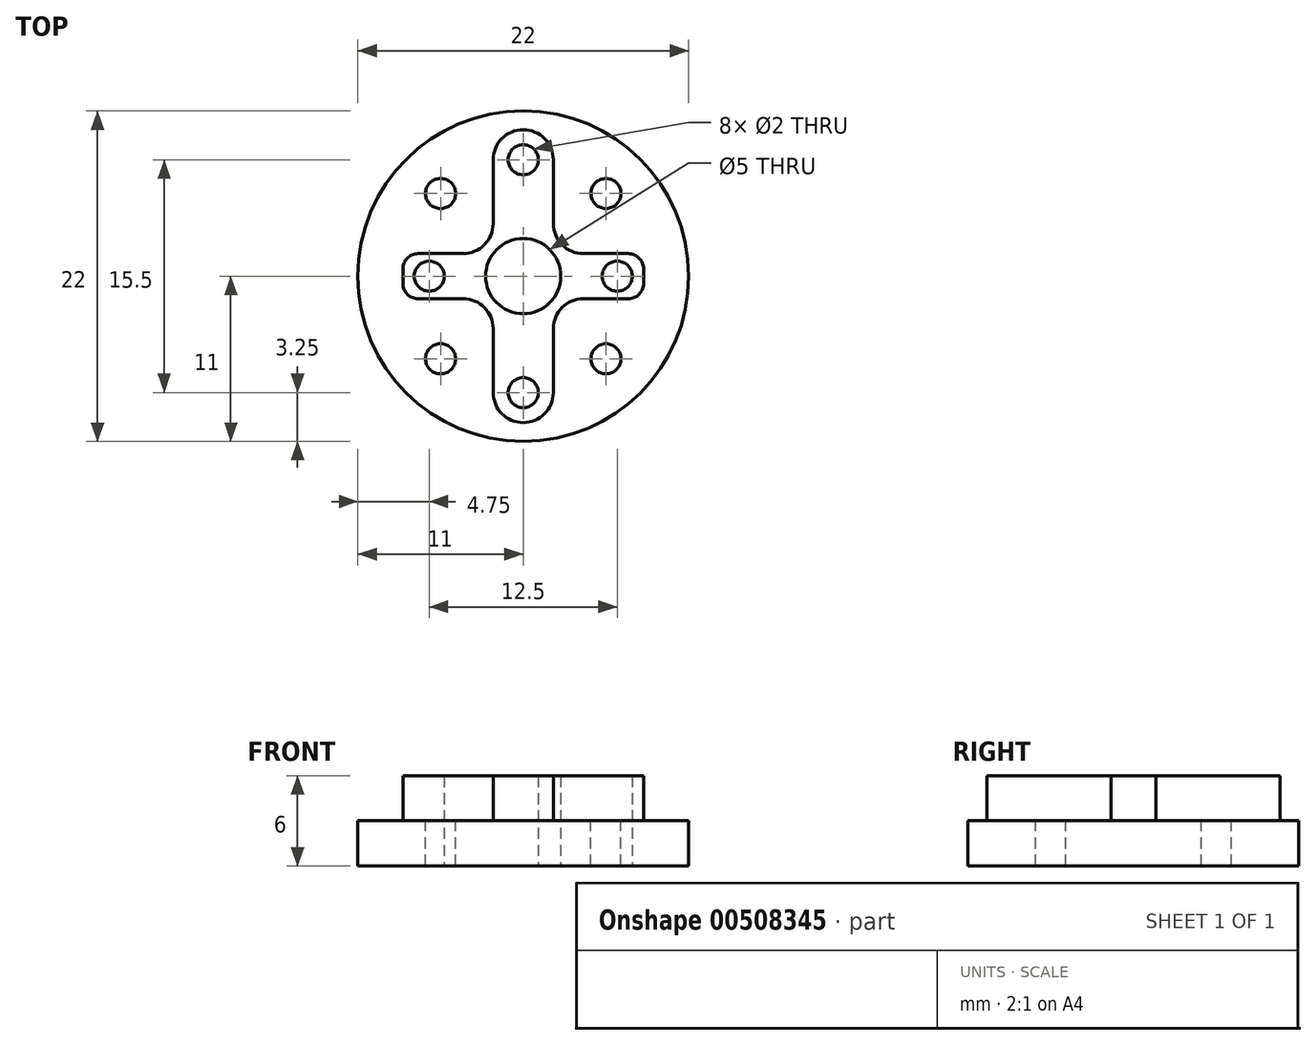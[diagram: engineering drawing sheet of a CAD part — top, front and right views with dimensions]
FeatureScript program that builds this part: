
annotation { "Feature Type Name" : "Feature", "Feature Type Description" : "" }
export const myFeature = defineFeature(function(context is Context, id is Id, definition is map)
    precondition{}
    {
        {
            var Q0;
            Q0=qCreatedBy(makeId("Top.planeOp"),FACE);
            var sketch = newSketch(context, id + "F0", { "sketchPlane" : qUnion([Q0])});
            skLineSegment(sketch, "E0", {"start": v(0, 15) * mm, "end": v(0, -15) * mm, "construction": true});
            skLineSegment(sketch, "E1", {"start": v(-15, 0) * mm, "end": v(15, 0) * mm, "construction": true});
            skCircle(sketch, "E2", {"center": v(0, 0) * mm, "radius": 2.5 * mm});
            skCircle(sketch, "E3", {"center": v(0, 7.75) * mm, "radius": 1 * mm});
            skCircle(sketch, "E4", {"center": v(6.25, 0) * mm, "radius": 1 * mm});
            skCircle(sketch, "E5.MirrorC", {"center": v(-6.25, 0) * mm, "radius": 1 * mm});
            skCircle(sketch, "E6.MirrorC", {"center": v(0, -7.75) * mm, "radius": 1 * mm});
            skLineSegment(sketch, "E7", {"start": v(2, 3.5) * mm, "end": v(2, 7.75) * mm});
            skLineSegment(sketch, "E8", {"start": v(4, 1.5) * mm, "end": v(7, 1.5) * mm});
            skPoint(sketch, "E9.visualSharp", {"position": v(2, 1.5) * mm});
            skArc(sketch, "E9.filletArc", {"start": v(2, 3.5) * mm, "mid": v(2.59, 2.09) * mm, "end": v(4, 1.5) * mm});
            skLineSegment(sketch, "E10.MirrorCS", {"start": v(-2, 3.5) * mm, "end": v(-2, 7.75) * mm});
            skArc(sketch, "E11.MirrorCS", {"start": v(-2, 3.5) * mm, "mid": v(-2.59, 2.09) * mm, "end": v(-4, 1.5) * mm});
            skLineSegment(sketch, "E12.MirrorCS", {"start": v(4, -1.5) * mm, "end": v(7, -1.5) * mm});
            skArc(sketch, "E13.MirrorCS", {"start": v(2, -3.5) * mm, "mid": v(2.59, -2.09) * mm, "end": v(4, -1.5) * mm});
            skArc(sketch, "E14.MirrorCS", {"start": v(-2, -3.5) * mm, "mid": v(-2.59, -2.09) * mm, "end": v(-4, -1.5) * mm});
            skLineSegment(sketch, "E15", {"start": v(0, 9.75) * mm, "end": v(0, 9.75) * mm});
            skPoint(sketch, "E16.visualSharp", {"position": v(2, 9.75) * mm});
            skArc(sketch, "E16.filletArc", {"start": v(2, 7.75) * mm, "mid": v(1.41, 9.16) * mm, "end": v(0, 9.75) * mm});
            skPoint(sketch, "E17.visualSharp", {"position": v(-2, 9.75) * mm});
            skArc(sketch, "E17.filletArc", {"start": v(0, 9.75) * mm, "mid": v(-1.41, 9.16) * mm, "end": v(-2, 7.75) * mm});
            skArc(sketch, "E18.MirrorCS", {"start": v(0, -9.75) * mm, "mid": v(-1.41, -9.16) * mm, "end": v(-2, -7.75) * mm});
            skArc(sketch, "E19.MirrorCS", {"start": v(2, -7.75) * mm, "mid": v(1.41, -9.16) * mm, "end": v(0, -9.75) * mm});
            skLineSegment(sketch, "E20.MirrorCS", {"start": v(2, -3.5) * mm, "end": v(2, -7.75) * mm});
            skLineSegment(sketch, "E21.MirrorCS", {"start": v(-2, -3.5) * mm, "end": v(-2, -7.75) * mm});
            skLineSegment(sketch, "E22", {"start": v(8, -0.5) * mm, "end": v(8, 0.5) * mm});
            skPoint(sketch, "E23.visualSharp", {"position": v(8, 1.5) * mm});
            skArc(sketch, "E23.filletArc", {"start": v(8, 0.5) * mm, "mid": v(7.7, 1.2) * mm, "end": v(7, 1.5) * mm});
            skPoint(sketch, "E24.visualSharp", {"position": v(8, -1.5) * mm});
            skArc(sketch, "E24.filletArc", {"start": v(7, -1.5) * mm, "mid": v(7.7, -1.2) * mm, "end": v(8, -0.5) * mm});
            skLineSegment(sketch, "E25.MirrorCS", {"start": v(-4, 1.5) * mm, "end": v(-7, 1.5) * mm});
            skLineSegment(sketch, "E26.MirrorCS", {"start": v(-8, -0.5) * mm, "end": v(-8, 0.5) * mm});
            skArc(sketch, "E27.MirrorCS", {"start": v(-7, -1.5) * mm, "mid": v(-7.7, -1.2) * mm, "end": v(-8, -0.5) * mm});
            skLineSegment(sketch, "E28.MirrorCS", {"start": v(-4, -1.5) * mm, "end": v(-7, -1.5) * mm});
            skArc(sketch, "E29.MirrorCS", {"start": v(-8, 0.5) * mm, "mid": v(-7.7, 1.2) * mm, "end": v(-7, 1.5) * mm});
            skSolve(sketch);
        }
        {
            var Q0;
            Q0=makeQuery(id+"F0.imprint","IMPRINT",FACE,{"disambiguationData":[TD([[makeQuery(id+"F0.imprint","IMPRINT",EDGE,{"derivedFrom":sQuery(id+"F0.wireOp",EDGE,"E2")}),-1.0]])]});
            extrude(context, id + "F1", {"entities" : qUnion([Q0]), "depth" : 3 * mm, "offsetDistance" : 25 * mm});
        }
        {
            var Q0;
            Q0=makeQuery(id+"F1.opExtrude","CAP_FACE",FACE,{"disambiguationData":[OSD([sQuery(id+"F0.wireOp",EDGE,"E2"),sQuery(id+"F0.wireOp",EDGE,"E3"),sQuery(id+"F0.wireOp",EDGE,"E4"),sQuery(id+"F0.wireOp",EDGE,"E5.MirrorC"),sQuery(id+"F0.wireOp",EDGE,"E6.MirrorC"),sQuery(id+"F0.wireOp",EDGE,"E7"),sQuery(id+"F0.wireOp",EDGE,"E8"),sQuery(id+"F0.wireOp",EDGE,"E9.filletArc"),sQuery(id+"F0.wireOp",EDGE,"E10.MirrorCS"),sQuery(id+"F0.wireOp",EDGE,"E11.MirrorCS"),sQuery(id+"F0.wireOp",EDGE,"E12.MirrorCS"),sQuery(id+"F0.wireOp",EDGE,"E13.MirrorCS"),sQuery(id+"F0.wireOp",EDGE,"E14.MirrorCS"),sQuery(id+"F0.wireOp",EDGE,"E18.MirrorCS"),sQuery(id+"F0.wireOp",EDGE,"E19.MirrorCS"),sQuery(id+"F0.wireOp",EDGE,"E16.filletArc"),sQuery(id+"F0.wireOp",EDGE,"E17.filletArc"),sQuery(id+"F0.wireOp",EDGE,"E20.MirrorCS"),sQuery(id+"F0.wireOp",EDGE,"E21.MirrorCS"),sQuery(id+"F0.wireOp",EDGE,"E22"),sQuery(id+"F0.wireOp",EDGE,"E23.filletArc"),sQuery(id+"F0.wireOp",EDGE,"E24.filletArc"),sQuery(id+"F0.wireOp",EDGE,"E25.MirrorCS"),sQuery(id+"F0.wireOp",EDGE,"E26.MirrorCS"),sQuery(id+"F0.wireOp",EDGE,"E27.MirrorCS"),sQuery(id+"F0.wireOp",EDGE,"E28.MirrorCS"),sQuery(id+"F0.wireOp",EDGE,"E29.MirrorCS")])],"isStart":true});
            var sketch = newSketch(context, id + "F2", { "sketchPlane" : qUnion([Q0])});
            skCircle(sketch, "E30", {"center": v(0, 0) * mm, "radius": 11 * mm});
            skLineSegment(sketch, "E31", {"start": v(0, 16.96) * mm, "end": v(0, -14.39) * mm, "construction": true});
            skCircle(sketch, "E32", {"center": v(-5.5, 5.5) * mm, "radius": 1 * mm});
            skLineSegment(sketch, "E33", {"start": v(-12.82, 0) * mm, "end": v(13.52, 0) * mm, "construction": true});
            skPoint(sketch, "E33.endSnap0", {"position": v(8, 0) * mm});
            skCircle(sketch, "E34.MirrorC", {"center": v(5.5, 5.5) * mm, "radius": 1 * mm});
            skCircle(sketch, "E35.MirrorC", {"center": v(5.5, -5.5) * mm, "radius": 1 * mm});
            skCircle(sketch, "E36.MirrorC", {"center": v(-5.5, -5.5) * mm, "radius": 1 * mm});
            skSolve(sketch);
        }
        {
            var Q0;
            Q0=makeQuery(id+"F2.imprint","IMPRINT",FACE,{"disambiguationData":[TD([[makeQuery(id+"F2.imprint","IMPRINT",EDGE,{"derivedFrom":sQuery(id+"F2.wireOp",EDGE,"E30")}),1.0]])]});
            var Q1;
            Q1=makeQuery(id+"F2.imprint","IMPRINT",FACE,{"disambiguationData":[TD([[makeQuery(id+"F2.imprint","IMPRINT",EDGE,{"derivedFrom":makeQuery(id+"F1.opExtrude","CAP_EDGE",EDGE,{"disambiguationData":[OSD([sQuery(id+"F0.wireOp",EDGE,"E2")])],"isStart":true})}),1.0]])]});
            extrude(context, id + "F3", {"entities" : qUnion([Q0, Q1]), "operationType" : NewBodyOperationType.ADD, "depth" : 3 * mm, "offsetDistance" : 25 * mm});
        }
    });
